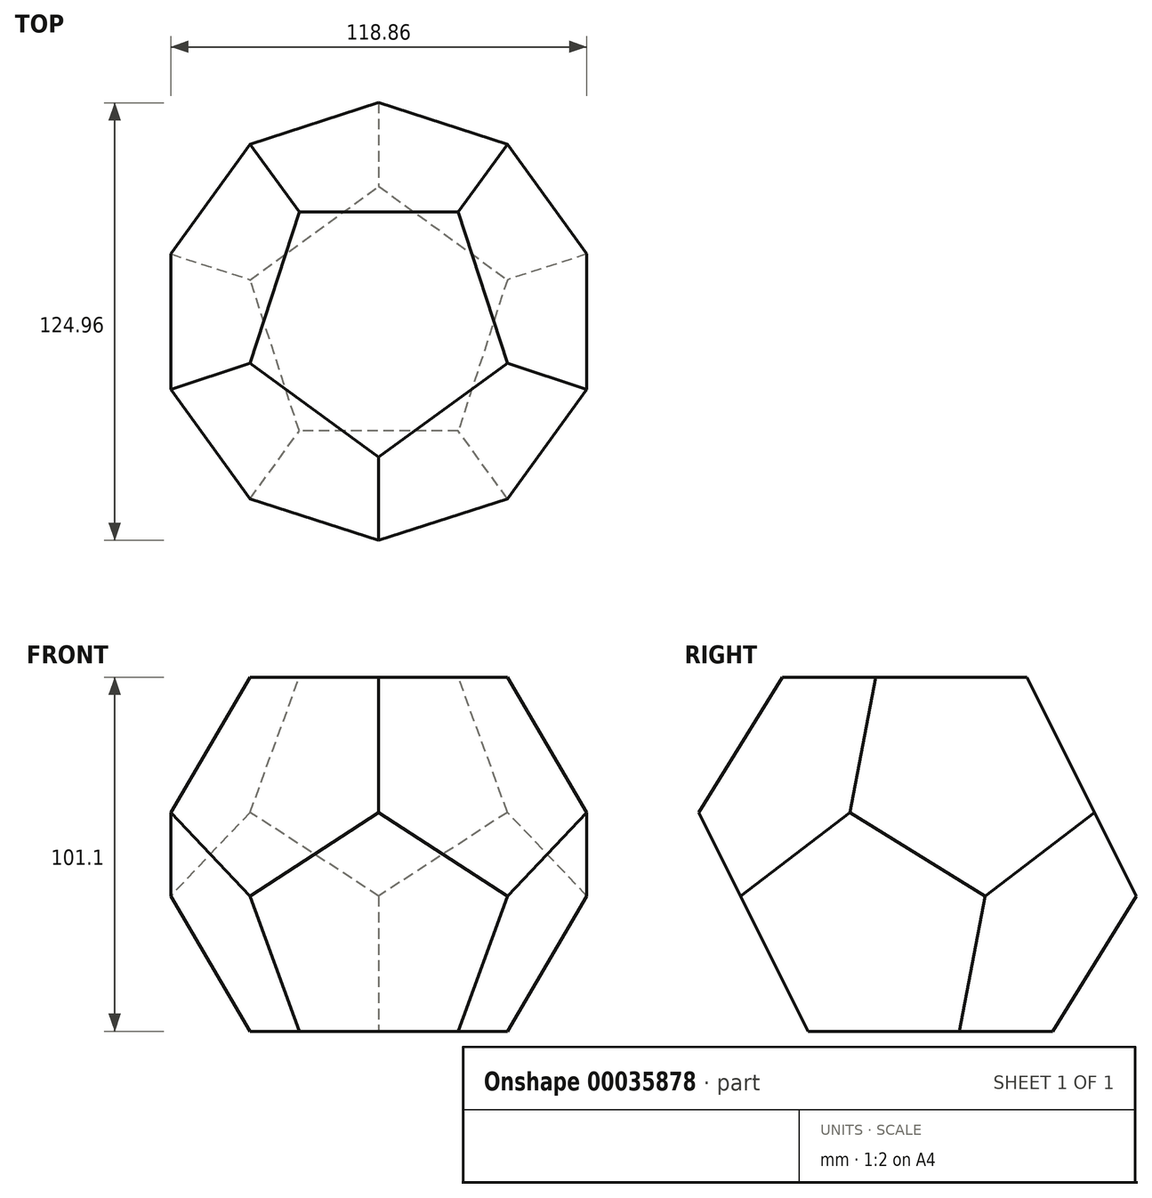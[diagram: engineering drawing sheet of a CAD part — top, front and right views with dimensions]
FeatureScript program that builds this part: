
annotation { "Feature Type Name" : "Feature", "Feature Type Description" : "" }
export const myFeature = defineFeature(function(context is Context, id is Id, definition is map)
    precondition{}
    {
        {
            var Q0;
            Q0=qCreatedBy(makeId("Right.planeOp"),FACE);
            var sketch = newSketch(context, id + "F0", { "sketchPlane" : qUnion([Q0])});
            skLineSegment(sketch, "E0.0", {"start": v(0, 133) * mm, "end": v(-82.2, 0) * mm});
            skPoint(sketch, "E1.orphan", {"position": v(-50.8, 50.8) * mm});
            skPoint(sketch, "E2.orphan", {"position": v(-31.4, 82.2) * mm});
            skLineSegment(sketch, "E3", {"start": v(0, 82.2) * mm, "end": v(0, 0) * mm});
            skLineSegment(sketch, "E4", {"start": v(0, 41.1) * mm, "end": v(84.2, 41.1) * mm});
            skSolve(sketch);
        }
        {
            var Q0;
            Q0=qCreatedBy(makeId("Top.planeOp"),FACE);
            var sketch = newSketch(context, id + "F1", { "sketchPlane" : qUnion([Q0])});
            skCircle(sketch, "E5.cCircle", {"center": v(0, 0) * mm, "radius": 66.5 * mm, "construction": true});
            skLineSegment(sketch, "E5.0", {"start": v(78.17, -25.4) * mm, "end": v(0, -82.2) * mm});
            skLineSegment(sketch, "E5.1", {"start": v(0, -82.2) * mm, "end": v(-78.17, -25.4) * mm});
            skLineSegment(sketch, "E5.2", {"start": v(-78.17, -25.4) * mm, "end": v(-48.31, 66.5) * mm});
            skLineSegment(sketch, "E5.3", {"start": v(-48.31, 66.5) * mm, "end": v(48.31, 66.5) * mm});
            skLineSegment(sketch, "E5.4", {"start": v(48.31, 66.5) * mm, "end": v(78.17, -25.4) * mm});
            skPoint(sketch, "E5.0.midPoint", {"position": v(39.09, -53.8) * mm});
            skSolve(sketch);
        }
        {
            var Q1;
            Q1=qSketchRegion(id+"F1",true);
            var Q2;
            Q2=sQuery(id+"F0.wireOp",VERTEX,"E0.0.start");
            loft(context, id + "F2", {"sheetProfilesArray" : [{ "sheetProfileEntities" : qUnion([Q1]) }, { "sheetProfileEntities" : qUnion([Q2]) }]});
        }
        {
            var Q0;
            Q0=makeQuery(id+"F2.opLoft","SWEPT_BODY",BODY,{"disambiguationData":[OSD([makeQuery(id+"F1.imprint","IMPRINT",FACE,{"disambiguationData":[TD([[makeQuery(id+"F1.imprint","IMPRINT",EDGE,{"derivedFrom":sQuery(id+"F1.wireOp",EDGE,"E5.0")}),-1.0]])]})])]});
            var Q1;
            Q1=sQuery(id+"F0.wireOp",EDGE,"E4");
            transform(context, id + "F3", {"entities" : qUnion([Q0]), "transformType" : TransformType.ROTATION, "transformAxis" : qUnion([Q1]), "angle" : 180 * degree, "makeCopy" : true});
        }
        {
            var Q0;
            Q0=makeQuery(id+"F3.opPattern","COPY",BODY,{"derivedFrom":makeQuery(id+"F2.opLoft","SWEPT_BODY",BODY,{"disambiguationData":[OSD([makeQuery(id+"F1.imprint","IMPRINT",FACE,{"disambiguationData":[TD([[makeQuery(id+"F1.imprint","IMPRINT",EDGE,{"derivedFrom":sQuery(id+"F1.wireOp",EDGE,"E5.0")}),-1.0]])]})])]}),"instanceName":"1"});
            var Q1;
            Q1=sQuery(id+"F0.wireOp",EDGE,"E3");
            transform(context, id + "F4", {"entities" : qUnion([Q0]), "transformType" : TransformType.ROTATION, "transformAxis" : qUnion([Q1]), "angle" : 36 * degree, "makeCopy" : false});
        }
        {
            var Q0;
            Q0=makeQuery(id+"F2.opLoft","SWEPT_BODY",BODY,{"disambiguationData":[OSD([makeQuery(id+"F1.imprint","IMPRINT",FACE,{"disambiguationData":[TD([[makeQuery(id+"F1.imprint","IMPRINT",EDGE,{"derivedFrom":sQuery(id+"F1.wireOp",EDGE,"E5.0")}),-1.0]])]})])]});
            var Q1;
            Q1=makeQuery(id+"F3.opPattern","COPY",BODY,{"derivedFrom":makeQuery(id+"F2.opLoft","SWEPT_BODY",BODY,{"disambiguationData":[OSD([makeQuery(id+"F1.imprint","IMPRINT",FACE,{"disambiguationData":[TD([[makeQuery(id+"F1.imprint","IMPRINT",EDGE,{"derivedFrom":sQuery(id+"F1.wireOp",EDGE,"E5.0")}),-1.0]])]})])]}),"instanceName":"1"});
            booleanBodies(context, id + "F5", {"operationType" : BooleanOperationType.INTERSECTION, "tools" : qUnion([Q0, Q1])});
        }
        {
            var Q0;
            {var subQ0=makeQuery(id+"F2.opLoft","SWEPT_BODY",BODY,{"disambiguationData":[OSD([sQuery(id+"F0.wireOp",VERTEX,"E0.0.start"),makeQuery(id+"F1.imprint","IMPRINT",FACE,{"disambiguationData":[TD([[makeQuery(id+"F1.imprint","IMPRINT",EDGE,{"derivedFrom":sQuery(id+"F1.wireOp",EDGE,"E5.0")}),-1.0]])]})])]});Q0=makeQuery(id+"F5.opBoolean","INTERSECT",BODY,{"derivedFrom":[subQ0,makeQuery(id+"F3.opPattern","COPY",BODY,{"derivedFrom":subQ0,"instanceName":"1"})]});}
            var Q1;
            Q1=qCreatedBy(makeId("Origin.pointOp"),VERTEX);
            transform(context, id + "F6", {"entities" : qUnion([Q0]), "transformType" : TransformType.SCALE_UNIFORMLY, "scale" : 1.23, "makeCopy" : false, "scalePoint" : qUnion([Q1])});
        }
    });
